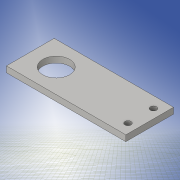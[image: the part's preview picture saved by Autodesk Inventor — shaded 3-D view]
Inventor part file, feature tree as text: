
AUTODESK INVENTOR PART (.ipt)
format: ipt  version: 2016 (Build 200138000, 138)  size: 125,440 bytes
history: native  units: in
note: dims shown in document units (in); Inventor stores cm internally (conversion verified against a paired STEP export)
features: sketch x3, extrude x2, hole x1
ambient origin geometry x8: Origin, YZ Plane, XZ Plane, XY Plane, X Axis, Y Axis, Z Axis, Center Point
bodies: Solid1 (feature_tree)
feature tree (6):
  extrude  "Extrusion1"  Depth=2.0in
  extrude  "Extrusion2"  Depth=0.25in
  hole  "Hole1"  [1 undecoded]
  sketch  "Sketch1"  dims[d0=5.0in d1=2.0in]
  sketch  "Sketch2"  dims[d2=0.25in d3=0.0in d4=1.125in]
  sketch  "Sketch3"  dims[d5=3.915in d6=0.25in d7=0.0in d8=1.068in d9=0.375in d10=0.375in d11=0.257in d12=0.75in d13=0.375in d14=0.25in d15=0.5635in d16=1.0in d17=0.8108in]
note: 1 required parameter value undecoded (feature->parameter linkage not recoverable at this tier; creation-order binding heuristic only, values carry confidence <= 0.55)
